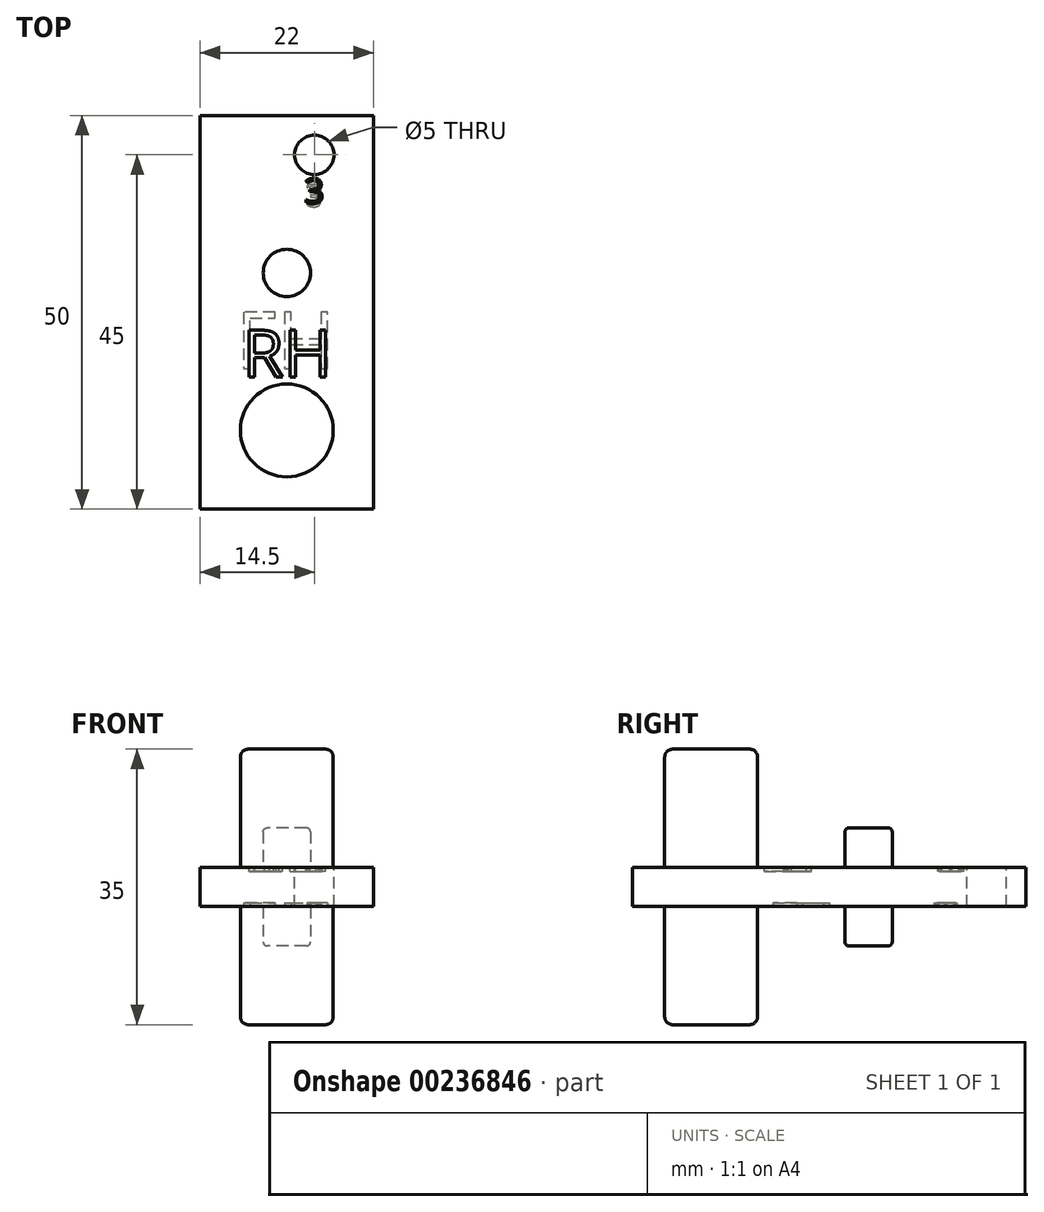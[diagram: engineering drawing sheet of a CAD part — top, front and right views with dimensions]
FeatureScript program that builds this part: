
annotation { "Feature Type Name" : "Feature", "Feature Type Description" : "" }
export const myFeature = defineFeature(function(context is Context, id is Id, definition is map)
    precondition{}
    {
        {
            var Q0;
            Q0=qCreatedBy(makeId("Top.planeOp"),FACE);
            var sketch = newSketch(context, id + "F0", { "sketchPlane" : qUnion([Q0])});
            skLineSegment(sketch, "E0.bottom", {"start": v(0, 0) * mm, "end": v(22, 0) * mm});
            skLineSegment(sketch, "E0.top", {"start": v(0, 50) * mm, "end": v(22, 50) * mm});
            skLineSegment(sketch, "E0.left", {"start": v(0, 0) * mm, "end": v(0, 50) * mm});
            skLineSegment(sketch, "E0.right", {"start": v(22, 0) * mm, "end": v(22, 50) * mm});
            skSolve(sketch);
        }
        {
            var Q0;
            Q0 = qSketchRegion(id + "F0", true);
            extrude(context, id + "F1", {"entities" : qUnion([Q0]), "depth" : 5 * mm});
        }
        {
            var Q0;
            Q0=makeQuery(id+"F1.opExtrude","CAP_FACE",FACE,{"disambiguationData":[OSD([sQuery(id+"F0.wireOp",EDGE,"E0.bottom"),sQuery(id+"F0.wireOp",EDGE,"E0.top"),sQuery(id+"F0.wireOp",EDGE,"E0.left"),sQuery(id+"F0.wireOp",EDGE,"E0.right")])],"isStart":false});
            var sketch = newSketch(context, id + "F2", { "sketchPlane" : qUnion([Q0])});
            skLineSegment(sketch, "E1", {"start": v(11, 50) * mm, "end": v(11, 0) * mm, "construction": true});
            skCircle(sketch, "E2", {"center": v(11, 10) * mm, "radius": 5.9 * mm});
            skSolve(sketch);
        }
        {
            var Q0;
            Q0 = qSketchRegion(id + "F2", true);
            extrude(context, id + "F3", {"entities" : qUnion([Q0]), "operationType" : NewBodyOperationType.ADD, "depth" : 15 * mm, "hasSecondDirection" : true, "secondDirectionOppositeDirection" : true, "secondDirectionDepth" : 20 * mm});
        }
        {
            var Q0;
            Q0=makeQuery(id+"F1.opExtrude","CAP_FACE",FACE,{"disambiguationData":[OSD([sQuery(id+"F0.wireOp",EDGE,"E0.bottom"),sQuery(id+"F0.wireOp",EDGE,"E0.top"),sQuery(id+"F0.wireOp",EDGE,"E0.left"),sQuery(id+"F0.wireOp",EDGE,"E0.right")])],"isStart":false});
            var sketch = newSketch(context, id + "F4", { "sketchPlane" : qUnion([Q0])});
            skLineSegment(sketch, "E3", {"start": v(11, 10) * mm, "end": v(11, 52.1) * mm, "construction": true});
            skCircle(sketch, "E4", {"center": v(11, 30) * mm, "radius": 3 * mm});
            skSolve(sketch);
        }
        {
            var Q0;
            Q0 = qSketchRegion(id + "F4", true);
            extrude(context, id + "F5", {"entities" : qUnion([Q0]), "operationType" : NewBodyOperationType.ADD, "depth" : 5 * mm, "hasSecondDirection" : true, "secondDirectionOppositeDirection" : true, "secondDirectionDepth" : 10 * mm});
        }
        {
            var Q0;
            Q0=makeQuery(id+"F1.opExtrude","CAP_FACE",FACE,{"disambiguationData":[OSD([sQuery(id+"F0.wireOp",EDGE,"E0.bottom"),sQuery(id+"F0.wireOp",EDGE,"E0.top"),sQuery(id+"F0.wireOp",EDGE,"E0.left"),sQuery(id+"F0.wireOp",EDGE,"E0.right")])],"isStart":false});
            var sketch = newSketch(context, id + "F6", { "sketchPlane" : qUnion([Q0])});
            skCircle(sketch, "E5", {"center": v(14.5, 45) * mm, "radius": 2.5 * mm});
            skPoint(sketch, "E6", {"position": v(11, 30) * mm});
            skSolve(sketch);
        }
        {
            var Q0;
            Q0 = qSketchRegion(id + "F6", true);
            extrude(context, id + "F7", {"entities" : qUnion([Q0]), "operationType" : NewBodyOperationType.REMOVE, "endBound" : BoundingType.THROUGH_ALL, "oppositeDirection" : true, "depth" : 25 * mm});
        }
        {
            var Q0;
            Q0=makeQuery(id+"F1.opExtrude","CAP_FACE",FACE,{"disambiguationData":[OSD([sQuery(id+"F0.wireOp",EDGE,"E0.bottom"),sQuery(id+"F0.wireOp",EDGE,"E0.top"),sQuery(id+"F0.wireOp",EDGE,"E0.left"),sQuery(id+"F0.wireOp",EDGE,"E0.right")])],"isStart":false});
            var sketch = newSketch(context, id + "F8", { "sketchPlane" : qUnion([Q0])});
            skText(sketch, "E7", { "text": "3", "fontName": "OpenSans-Regular.ttf"});
            skPoint(sketch, "E8", {"position": v(14.5, 45) * mm});
            const initialGuessF8  = {"E7": [0.01323, 0.03884, 1, 0, 0.00316]};
            skSetInitialGuess(sketch, initialGuessF8);
            skSolve(sketch);
        }
        {
            var Q0;
            Q0=makeQuery(id+"F8.imprint","IMPRINT",FACE,{"disambiguationData":[TD([[makeQuery(id+"F8.imprint","IMPRINT",EDGE,{"derivedFrom":sQuery(id+"F8.wireOp",EDGE,"E7.sketch_text.stroke-0")}),1.0]])]});
            var sketch = newSketch(context, id + "F9", { "sketchPlane" : qUnion([Q0])});
            skText(sketch, "E9", { "text": "RH", "fontName": "OpenSans-Regular.ttf"});
            const initialGuessF9  = {"E9": [0.0054, 0.01675, 1, 0, 0.00602]};
            skSetInitialGuess(sketch, initialGuessF9);
            skSolve(sketch);
        }
        {
            var Q0;
            Q0 = qSketchRegion(id + "F9", true);
            extrude(context, id + "F10", {"entities" : qUnion([Q0]), "operationType" : NewBodyOperationType.REMOVE, "oppositeDirection" : true, "depth" : 0.5 * mm});
        }
        {
            var Q0;
            Q0 = qSketchRegion(id + "F8", true);
            extrude(context, id + "F11", {"entities" : qUnion([Q0]), "operationType" : NewBodyOperationType.REMOVE, "oppositeDirection" : true, "depth" : 0.5 * mm});
        }
        {
            var Q0;
            Q0=makeQuery(id+"F1.opExtrude","CAP_FACE",FACE,{"disambiguationData":[OSD([sQuery(id+"F0.wireOp",EDGE,"E0.bottom"),sQuery(id+"F0.wireOp",EDGE,"E0.top"),sQuery(id+"F0.wireOp",EDGE,"E0.left"),sQuery(id+"F0.wireOp",EDGE,"E0.right")])],"isStart":true});
            var sketch = newSketch(context, id + "F12", { "sketchPlane" : qUnion([Q0])});
            skText(sketch, "E10", { "text": "LH", "fontName": "OpenSans-Regular.ttf"});
            skPoint(sketch, "E10.firstSnap0", {"position": v(22, -25) * mm});
            const initialGuessF12  = {"E10": [0.00452, -0.025, 1, 0, 0.00723]};
            skSetInitialGuess(sketch, initialGuessF12);
            skSolve(sketch);
        }
        {
            var Q0;
            Q0 = qSketchRegion(id + "F12", true);
            extrude(context, id + "F13", {"entities" : qUnion([Q0]), "operationType" : NewBodyOperationType.REMOVE, "oppositeDirection" : true, "depth" : 0.5 * mm});
        }
        {
            var Q0;
            Q0=makeQuery(id+"F1.opExtrude","CAP_FACE",FACE,{"disambiguationData":[OSD([sQuery(id+"F0.wireOp",EDGE,"E0.bottom"),sQuery(id+"F0.wireOp",EDGE,"E0.top"),sQuery(id+"F0.wireOp",EDGE,"E0.left"),sQuery(id+"F0.wireOp",EDGE,"E0.right")])],"isStart":true});
            var sketch = newSketch(context, id + "F14", { "sketchPlane" : qUnion([Q0])});
            skText(sketch, "E11", { "text": "3\n", "fontName": "OpenSans-Regular.ttf"});
            skPoint(sketch, "E12", {"position": v(14.5, -45) * mm});
            const initialGuessF14  = {"E11": [0.01338, -0.0412, 1, 0, 0.0028]};
            skSetInitialGuess(sketch, initialGuessF14);
            skSolve(sketch);
        }
        {
            var Q0;
            Q0 = qSketchRegion(id + "F14", true);
            extrude(context, id + "F15", {"entities" : qUnion([Q0]), "operationType" : NewBodyOperationType.REMOVE, "oppositeDirection" : true, "depth" : 0.5 * mm});
        }
        {
            var Q0;
            Q0=makeQuery(id+"F3.opExtrude","CAP_EDGE",EDGE,{"disambiguationData":[OSD([sQuery(id+"F2.wireOp",EDGE,"E2")])],"isStart":false});
            var Q1;
            Q1=makeQuery(id+"F3.opExtrude","CAP_EDGE",EDGE,{"disambiguationData":[OSD([sQuery(id+"F2.wireOp",EDGE,"E2")])],"isStart":true});
            fillet(context, id + "F16", {"entities" : qUnion([Q0, Q1]), "radius" : 1 * mm, "tangentPropagation" : true, "allowEdgeOverflow" : false});
        }
        {
            var Q0;
            Q0=makeQuery(id+"F5.opExtrude","CAP_EDGE",EDGE,{"disambiguationData":[OSD([sQuery(id+"F4.wireOp",EDGE,"E4")])],"isStart":false});
            var Q1;
            Q1=makeQuery(id+"F5.opExtrude","CAP_EDGE",EDGE,{"disambiguationData":[OSD([sQuery(id+"F4.wireOp",EDGE,"E4")])],"isStart":true});
            fillet(context, id + "F17", {"entities" : qUnion([Q0, Q1]), "radius" : 0.5 * mm, "tangentPropagation" : true, "allowEdgeOverflow" : false});
        }
    });
